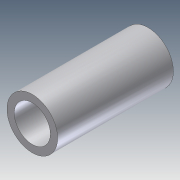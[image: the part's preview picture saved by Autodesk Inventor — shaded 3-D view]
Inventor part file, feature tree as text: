
AUTODESK INVENTOR PART (.ipt)
format: ipt  version: unknown  size: 163,840 bytes
history: native  units: in
note: dims shown in document units (in); Inventor stores cm internally (conversion verified against a paired STEP export)
features: extrude x1, sketch x1
ambient origin geometry x8: Origin, YZ Plane, XZ Plane, XY Plane, X Axis, Y Axis, Z Axis, Center Point
bodies: Solid1 (feature_tree)
feature tree (2):
  extrude  "Extrusion1"  Depth=0.125in
  sketch  "Sketch1"  dims[d0=0.875in d1=0.125in d2=2.0in d3=0.0in]
